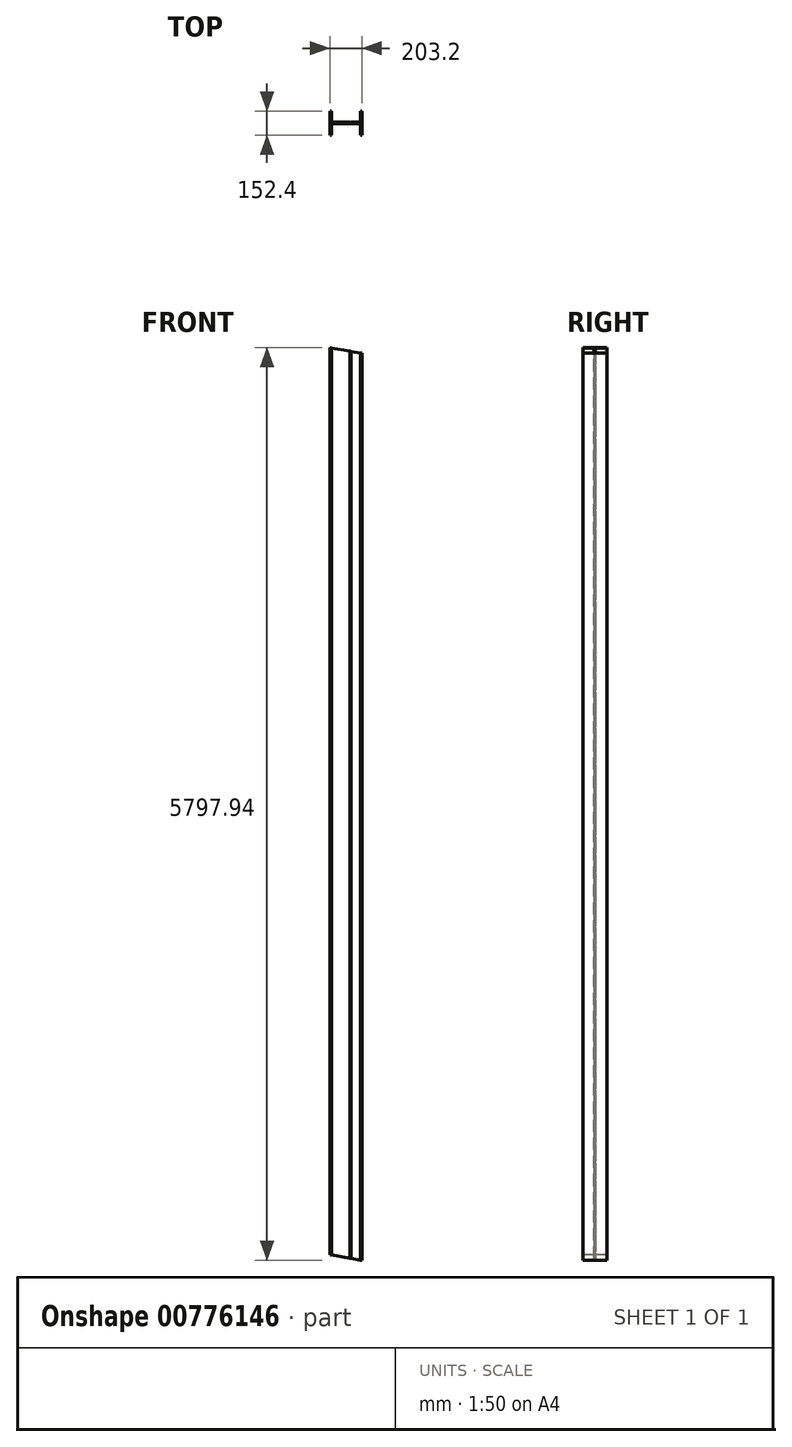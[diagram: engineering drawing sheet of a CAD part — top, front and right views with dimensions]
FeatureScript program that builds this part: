
annotation { "Feature Type Name" : "Feature", "Feature Type Description" : "" }
export const myFeature = defineFeature(function(context is Context, id is Id, definition is map)
    precondition{}
    {
        {
            var Q0;
            Q0=qCreatedBy(makeId("Top.planeOp"),FACE);
            var sketch = newSketch(context, id + "F0", { "sketchPlane" : qUnion([Q0])});
            skLineSegment(sketch, "E0", {"start": v(-301.4, -118.4) * mm, "end": v(-301.4, -118.4) * mm});
            skLineSegment(sketch, "E1", {"start": v(-227.15, 108.6) * mm, "end": v(220.95, 108.6) * mm, "construction": true});
            skLineSegment(sketch, "E2", {"start": v(0, 367.64) * mm, "end": v(0, -158.13) * mm, "construction": true});
            skLineSegment(sketch, "E3.0", {"start": v(-227.15, 32.4) * mm, "end": v(220.95, 32.4) * mm, "construction": true});
            skLineSegment(sketch, "E4.0", {"start": v(-227.15, 184.8) * mm, "end": v(220.95, 184.8) * mm, "construction": true});
            skLineSegment(sketch, "E5.0", {"start": v(-101.6, 184.8) * mm, "end": v(-101.6, 32.4) * mm});
            skLineSegment(sketch, "E6.0", {"start": v(101.6, 184.8) * mm, "end": v(101.6, 32.4) * mm});
            skLineSegment(sketch, "E7.0", {"start": v(-92.07, 103.84) * mm, "end": v(92.08, 103.84) * mm});
            skLineSegment(sketch, "E8.0", {"start": v(-92.07, 113.37) * mm, "end": v(92.08, 113.37) * mm});
            skLineSegment(sketch, "E9.0", {"start": v(92.08, 184.8) * mm, "end": v(92.08, 113.37) * mm});
            skLineSegment(sketch, "E10.0", {"start": v(-92.07, 184.8) * mm, "end": v(-92.07, 113.37) * mm});
            skLineSegment(sketch, "E11.trimOffspring", {"start": v(-92.07, 103.84) * mm, "end": v(-92.07, 32.4) * mm});
            skLineSegment(sketch, "E12.trimOffspring", {"start": v(92.08, 103.84) * mm, "end": v(92.08, 32.4) * mm});
            skLineSegment(sketch, "E13", {"start": v(-101.6, 184.8) * mm, "end": v(-92.07, 184.8) * mm});
            skLineSegment(sketch, "E14", {"start": v(-101.6, 32.4) * mm, "end": v(-92.07, 32.4) * mm});
            skLineSegment(sketch, "E15", {"start": v(92.08, 32.4) * mm, "end": v(101.6, 32.4) * mm});
            skLineSegment(sketch, "E16", {"start": v(92.08, 184.8) * mm, "end": v(101.6, 184.8) * mm});
            skSolve(sketch);
        }
        {
            var Q0;
            Q0=makeQuery(id+"F0.imprint","IMPRINT",FACE,{"disambiguationData":[TD([[makeQuery(id+"F0.imprint","IMPRINT",EDGE,{"derivedFrom":sQuery(id+"F0.wireOp",EDGE,"E5.0")}),1.0]])]});
            extrude(context, id + "F1", {"entities" : qUnion([Q0]), "depth" : 5797.94 * mm, "offsetDistance" : 25 * mm});
        }
        {
            var Q0;
            Q0=makeQuery(id+"F1.opExtrude","SWEPT_FACE",FACE,{"disambiguationData":[OSD([sQuery(id+"F0.wireOp",EDGE,"E14")])]});
            var sketch = newSketch(context, id + "F2", { "sketchPlane" : qUnion([Q0])});
            skLineSegment(sketch, "E17", {"start": v(-101.6, 0) * mm, "end": v(-101.6, 35.83) * mm});
            skPoint(sketch, "E18", {"position": v(0, 0) * mm});
            skLineSegment(sketch, "E19", {"start": v(0, 0) * mm, "end": v(0, 119.22) * mm, "construction": true});
            skLineSegment(sketch, "E20", {"start": v(101.6, 0) * mm, "end": v(-101.6, 35.83) * mm});
            skLineSegment(sketch, "E21", {"start": v(101.6, 0) * mm, "end": v(-101.6, 0) * mm});
            skLineSegment(sketch, "E22", {"start": v(575.01, 2898.97) * mm, "end": v(-683.12, 2898.97) * mm, "construction": true});
            skPoint(sketch, "E22.startSnap0", {"position": v(-101.6, 2898.97) * mm});
            skLineSegment(sketch, "E23", {"start": v(0, 0) * mm, "end": v(0, 6309.1) * mm, "construction": true});
            skLineSegment(sketch, "E24.MirrorCS", {"start": v(101.6, 5797.94) * mm, "end": v(-101.6, 5797.94) * mm});
            skLineSegment(sketch, "E25.MirrorCS", {"start": v(101.6, 5797.94) * mm, "end": v(101.6, 5762.11) * mm});
            skLineSegment(sketch, "E26.MirrorCS", {"start": v(-101.6, 5797.94) * mm, "end": v(101.6, 5762.11) * mm});
            skSolve(sketch);
        }
        {
            var Q0;
            Q0=makeQuery(id+"F1.opExtrude","CAP_FACE",FACE,{"disambiguationData":[OSD([sQuery(id+"F0.wireOp",EDGE,"E5.0"),sQuery(id+"F0.wireOp",EDGE,"E6.0"),sQuery(id+"F0.wireOp",EDGE,"E7.0"),sQuery(id+"F0.wireOp",EDGE,"E8.0"),sQuery(id+"F0.wireOp",EDGE,"E9.0"),sQuery(id+"F0.wireOp",EDGE,"E10.0"),sQuery(id+"F0.wireOp",EDGE,"E11.trimOffspring"),sQuery(id+"F0.wireOp",EDGE,"E12.trimOffspring"),sQuery(id+"F0.wireOp",EDGE,"E13"),sQuery(id+"F0.wireOp",EDGE,"E14"),sQuery(id+"F0.wireOp",EDGE,"E15"),sQuery(id+"F0.wireOp",EDGE,"E16")])],"isStart":false});
            var sketch = newSketch(context, id + "F3", { "sketchPlane" : qUnion([Q0])});
            skLineSegment(sketch, "E27", {"start": v(-101.6, 184.8) * mm, "end": v(101.6, 184.8) * mm, "construction": true});
            skLineSegment(sketch, "E28", {"start": v(101.6, 184.8) * mm, "end": v(101.6, -63) * mm, "construction": true});
            skLineSegment(sketch, "E29.0", {"start": v(33.87, 184.8) * mm, "end": v(33.87, -63) * mm, "construction": true});
            skLineSegment(sketch, "E30", {"start": v(24.7, 113.37) * mm, "end": v(33.87, 113.37) * mm});
            skLineSegment(sketch, "E31", {"start": v(33.87, 103.84) * mm, "end": v(24.7, 103.84) * mm});
            skLineSegment(sketch, "E32", {"start": v(-7.38, 184.8) * mm, "end": v(-76.36, 304.3) * mm});
            skLineSegment(sketch, "E33.0", {"start": v(24.82, 113.17) * mm, "end": v(24.7, 113.37) * mm});
            skLineSegment(sketch, "E34.0", {"start": v(24.82, 113.17) * mm, "end": v(33.98, 113.17) * mm});
            skLineSegment(sketch, "E35", {"start": v(33.87, 113.37) * mm, "end": v(33.98, 113.17) * mm});
            skLineSegment(sketch, "E36", {"start": v(-101.6, 108.6) * mm, "end": v(187.84, 108.6) * mm, "construction": true});
            skLineSegment(sketch, "E37.MirrorCS", {"start": v(24.82, 104.04) * mm, "end": v(24.7, 103.84) * mm});
            skLineSegment(sketch, "E38.MirrorCS", {"start": v(33.87, 103.84) * mm, "end": v(33.98, 104.04) * mm});
            skLineSegment(sketch, "E39.MirrorCS", {"start": v(24.82, 104.04) * mm, "end": v(33.98, 104.04) * mm});
            skLineSegment(sketch, "E40.trimOffspring", {"start": v(-16.54, 184.8) * mm, "end": v(-83.24, 300.33) * mm});
            skPoint(sketch, "E41.orphan", {"position": v(-83.24, -83.11) * mm});
            skPoint(sketch, "E42.MirrorCS.end.orphan", {"position": v(-76.36, -87.08) * mm});
            skPoint(sketch, "E42.MirrorCS.start.orphan", {"position": v(33.87, 103.84) * mm});
            skPoint(sketch, "E43.orphan", {"position": v(27, 107.81) * mm});
            skPoint(sketch, "E44.orphan", {"position": v(34.16, 104.35) * mm});
            skPoint(sketch, "E45.orphan", {"position": v(92.08, 104.04) * mm});
            skPoint(sketch, "E46.orphan", {"position": v(-92.07, 104.04) * mm});
            skPoint(sketch, "E47.orphan", {"position": v(27, 109.4) * mm});
            skPoint(sketch, "E48.orphan", {"position": v(34.16, 112.86) * mm});
            skPoint(sketch, "E49.orphan", {"position": v(92.08, 113.17) * mm});
            skPoint(sketch, "E50.orphan", {"position": v(-92.07, 113.17) * mm});
            skSolve(sketch);
        }
        {
            var Q0;
            Q0=makeQuery(id+"F3.imprint","IMPRINT",FACE,{"disambiguationData":[TD([[makeQuery(id+"F3.imprint","IMPRINT",EDGE,{"derivedFrom":sQuery(id+"F3.wireOp",EDGE,"E30")}),-1.0]])]});
            var Q1;
            Q1=makeQuery(id+"F3.imprint","IMPRINT",FACE,{"disambiguationData":[TD([[makeQuery(id+"F3.imprint","IMPRINT",EDGE,{"derivedFrom":sQuery(id+"F3.wireOp",EDGE,"E31")}),1.0]])]});
            extrude(context, id + "F4", {"entities" : qUnion([Q0, Q1]), "operationType" : NewBodyOperationType.REMOVE, "endBound" : BoundingType.THROUGH_ALL, "oppositeDirection" : true, "depth" : 25 * mm, "offsetDistance" : 25 * mm});
        }
        {
            var Q0;
            {var subQ3=sQuery(id+"F2.wireOp",EDGE,"E25.MirrorCS");Q0=makeQuery(id+"F2.imprint","IMPRINT",FACE,{"disambiguationData":[TD([[makeQuery(id+"F2.imprint","IMPRINT",EDGE,{"derivedFrom":subQ3}),-1.0]])]});}
            var Q1;
            {var subQ0=sQuery(id+"F2.wireOp",EDGE,"E26.MirrorCS");var subQ1=sQuery(id+"F2.wireOp",EDGE,"E24.MirrorCS");var subQ2=sQuery(id+"F0.wireOp",EDGE,"E14");var subQ3=makeQuery(id+"F2.imprint","INTERSECT",VERTEX,{"derivedFrom":[makeQuery(id+"F1.opExtrude","SWEPT_EDGE",EDGE,{"disambiguationData":[OSD([sQuery(id+"F0.wireOp",EDGE,"E5.0"),subQ2])]}),subQ1,subQ0]});Q1=makeQuery(id+"F2.imprint","IMPRINT",FACE,{"disambiguationData":[TD([[makeQuery(id+"F2.imprint","IMPRINT",EDGE,{"disambiguationData":[TD([[subQ3,-1.0]])],"derivedFrom":subQ1}),-1.0]])]});}
            var Q2;
            {var subQ0=sQuery(id+"F2.wireOp",EDGE,"E21");var subQ1=sQuery(id+"F2.wireOp",EDGE,"E20");var subQ2=makeQuery(id+"F2.imprint","INTERSECT",VERTEX,{"derivedFrom":[subQ1,subQ0]});Q2=makeQuery(id+"F2.imprint","IMPRINT",FACE,{"disambiguationData":[TD([[makeQuery(id+"F2.imprint","IMPRINT",EDGE,{"disambiguationData":[TD([[subQ2,-1.0]])],"derivedFrom":subQ1}),1.0]])]});}
            var Q3;
            {var subQ0=sQuery(id+"F2.wireOp",EDGE,"E17");Q3=makeQuery(id+"F2.imprint","IMPRINT",FACE,{"disambiguationData":[TD([[makeQuery(id+"F2.imprint","IMPRINT",EDGE,{"derivedFrom":subQ0}),1.0]])]});}
            extrude(context, id + "F5", {"entities" : qUnion([Q0, Q1, Q2, Q3]), "operationType" : NewBodyOperationType.REMOVE, "endBound" : BoundingType.THROUGH_ALL, "oppositeDirection" : true, "depth" : 25 * mm, "offsetDistance" : 25 * mm});
        }
    });
